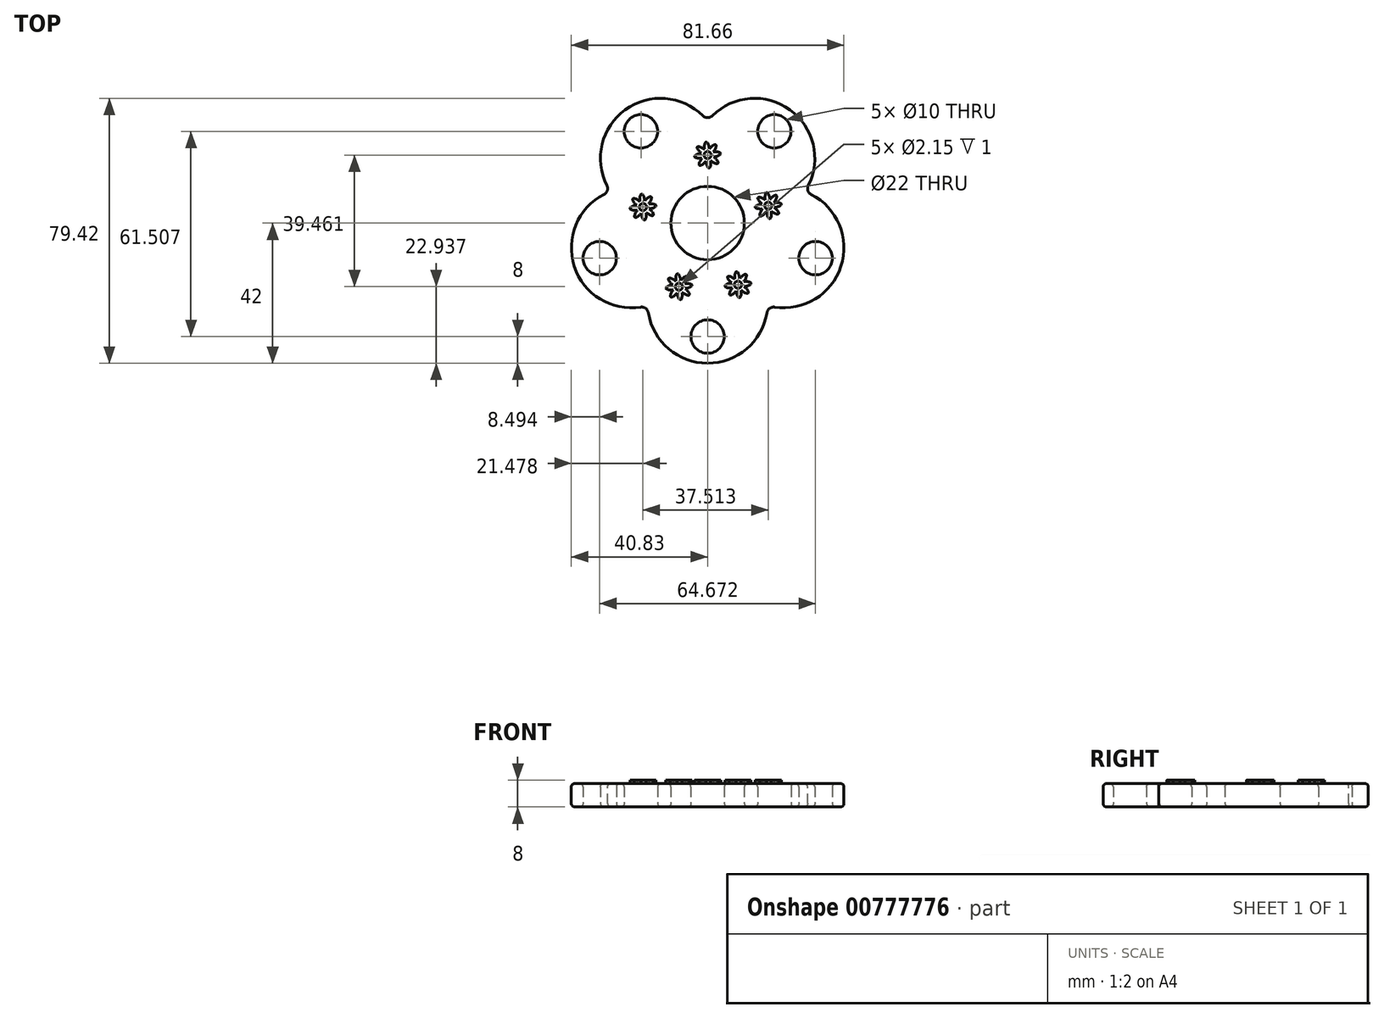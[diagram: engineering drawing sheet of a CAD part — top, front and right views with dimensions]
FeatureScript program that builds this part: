
annotation { "Feature Type Name" : "Feature", "Feature Type Description" : "" }
export const myFeature = defineFeature(function(context is Context, id is Id, definition is map)
    precondition{}
    {
        {
            var Q0;
            Q0=qCreatedBy(makeId("Top.planeOp"),FACE);
            var sketch = newSketch(context, id + "F0", { "sketchPlane" : qUnion([Q0])});
            skCircle(sketch, "E0.cCircle", {"center": v(0, 0) * mm, "radius": 24 * mm, "construction": true});
            skPoint(sketch, "E0.0.midPoint", {"position": v(14.1, 19.42) * mm});
            skArc(sketch, "E1", {"start": v(0, 30.6) * mm, "mid": v(-24.69, 33.98) * mm, "end": v(-29.1, 9.45) * mm});
            skArc(sketch, "E2", {"start": v(29.1, 9.45) * mm, "mid": v(24.69, 33.98) * mm, "end": v(0, 30.6) * mm});
            skArc(sketch, "E3", {"start": v(17.98, -24.75) * mm, "mid": v(39.94, -12.98) * mm, "end": v(29.1, 9.45) * mm});
            skArc(sketch, "E4", {"start": v(-17.98, -24.75) * mm, "mid": v(0, -42) * mm, "end": v(17.98, -24.75) * mm});
            skArc(sketch, "E5", {"start": v(-29.1, 9.45) * mm, "mid": v(-39.94, -12.98) * mm, "end": v(-17.98, -24.75) * mm});
            skCircle(sketch, "E6", {"center": v(0, 0) * mm, "radius": 30.6 * mm, "construction": true});
            skCircle(sketch, "E7", {"center": v(0, 0) * mm, "radius": 11 * mm});
            skCircle(sketch, "E8", {"center": v(-19.98, 27.5) * mm, "radius": 5 * mm});
            skCircle(sketch, "E9", {"center": v(19.98, 27.5) * mm, "radius": 5 * mm});
            skCircle(sketch, "E10", {"center": v(32.34, -10.5) * mm, "radius": 5 * mm});
            skCircle(sketch, "E11", {"center": v(0, -34) * mm, "radius": 5 * mm});
            skCircle(sketch, "E12", {"center": v(-32.34, -10.5) * mm, "radius": 5 * mm});
            skCircle(sketch, "E13", {"center": v(0, 0) * mm, "radius": 34 * mm, "construction": true});
            skLineSegment(sketch, "E14", {"start": v(0, 0) * mm, "end": v(0, 61.86) * mm, "construction": true});
            skLineSegment(sketch, "E15", {"start": v(0, 0) * mm, "end": v(37.88, 52.14) * mm, "construction": true});
            skLineSegment(sketch, "E16", {"start": v(0, 0) * mm, "end": v(75.05, -24.39) * mm, "construction": true});
            skLineSegment(sketch, "E17", {"start": v(0, 0) * mm, "end": v(0, -39) * mm, "construction": true});
            skLineSegment(sketch, "E18", {"start": v(0, 0) * mm, "end": v(-66.61, -21.64) * mm, "construction": true});
            skLineSegment(sketch, "E19", {"start": v(0, 0) * mm, "end": v(-34.54, 47.54) * mm, "construction": true});
            skSolve(sketch);
        }
        {
            var Q0;
            Q0=qSketchRegion(id+"F0",true);
            extrude(context, id + "F1", {"entities" : qUnion([Q0]), "depth" : 7 * mm, "offsetDistance" : 25.4 * mm});
        }
        {
            var Q0;
            Q0=makeQuery(id+"F1.opExtrude","SWEPT_EDGE",EDGE,{"disambiguationData":[OSD([sQuery(id+"F0.wireOp",EDGE,"E3"),sQuery(id+"F0.wireOp",EDGE,"E4")])]});
            var Q1;
            Q1=makeQuery(id+"F1.opExtrude","SWEPT_EDGE",EDGE,{"disambiguationData":[OSD([sQuery(id+"F0.wireOp",EDGE,"E2"),sQuery(id+"F0.wireOp",EDGE,"E3")])]});
            var Q2;
            Q2=makeQuery(id+"F1.opExtrude","SWEPT_EDGE",EDGE,{"disambiguationData":[OSD([sQuery(id+"F0.wireOp",EDGE,"E1"),sQuery(id+"F0.wireOp",EDGE,"E2")])]});
            var Q3;
            Q3=makeQuery(id+"F1.opExtrude","SWEPT_EDGE",EDGE,{"disambiguationData":[OSD([sQuery(id+"F0.wireOp",EDGE,"E1"),sQuery(id+"F0.wireOp",EDGE,"E5")])]});
            var Q4;
            Q4=makeQuery(id+"F1.opExtrude","SWEPT_EDGE",EDGE,{"disambiguationData":[OSD([sQuery(id+"F0.wireOp",EDGE,"E4"),sQuery(id+"F0.wireOp",EDGE,"E5")])]});
            fillet(context, id + "F2", {"entities" : qUnion([Q0, Q1, Q2, Q3, Q4]), "radius" : 2 * mm, "tangentPropagation" : true, "allowEdgeOverflow" : false});
        }
        {
            var Q0;
            Q0=makeQuery(id+"F1.opExtrude","CAP_FACE",FACE,{"disambiguationData":[OSD([sQuery(id+"F0.wireOp",EDGE,"E1"),sQuery(id+"F0.wireOp",EDGE,"E2"),sQuery(id+"F0.wireOp",EDGE,"E3"),sQuery(id+"F0.wireOp",EDGE,"E4"),sQuery(id+"F0.wireOp",EDGE,"E5"),sQuery(id+"F0.wireOp",EDGE,"E7"),sQuery(id+"F0.wireOp",EDGE,"E8"),sQuery(id+"F0.wireOp",EDGE,"E9"),sQuery(id+"F0.wireOp",EDGE,"E10"),sQuery(id+"F0.wireOp",EDGE,"E11"),sQuery(id+"F0.wireOp",EDGE,"E12")])],"isStart":false});
            var Q1;
            Q1=makeQuery(id+"F1.opExtrude","CAP_FACE",FACE,{"disambiguationData":[OSD([sQuery(id+"F0.wireOp",EDGE,"E1"),sQuery(id+"F0.wireOp",EDGE,"E2"),sQuery(id+"F0.wireOp",EDGE,"E3"),sQuery(id+"F0.wireOp",EDGE,"E4"),sQuery(id+"F0.wireOp",EDGE,"E5"),sQuery(id+"F0.wireOp",EDGE,"E7"),sQuery(id+"F0.wireOp",EDGE,"E8"),sQuery(id+"F0.wireOp",EDGE,"E9"),sQuery(id+"F0.wireOp",EDGE,"E10"),sQuery(id+"F0.wireOp",EDGE,"E11"),sQuery(id+"F0.wireOp",EDGE,"E12")])],"isStart":true});
            fillet(context, id + "F3", {"entities" : qUnion([Q0, Q1]), "radius" : 1 * mm, "tangentPropagation" : true, "allowEdgeOverflow" : false});
        }
        {
            var Q0;
            Q0=makeQuery(id+"F1.opExtrude","CAP_FACE",FACE,{"disambiguationData":[OSD([sQuery(id+"F0.wireOp",EDGE,"E1"),sQuery(id+"F0.wireOp",EDGE,"E2"),sQuery(id+"F0.wireOp",EDGE,"E3"),sQuery(id+"F0.wireOp",EDGE,"E4"),sQuery(id+"F0.wireOp",EDGE,"E5"),sQuery(id+"F0.wireOp",EDGE,"E7"),sQuery(id+"F0.wireOp",EDGE,"E8"),sQuery(id+"F0.wireOp",EDGE,"E9"),sQuery(id+"F0.wireOp",EDGE,"E10"),sQuery(id+"F0.wireOp",EDGE,"E11"),sQuery(id+"F0.wireOp",EDGE,"E12")])],"isStart":false});
            var sketch = newSketch(context, id + "F4", { "sketchPlane" : qUnion([Q0])});
            skEllipticalArc(sketch, "E20", {});
            skEllipticalArc(sketch, "E21.1.0", {});
            skEllipticalArc(sketch, "E21.2.0", {});
            skEllipticalArc(sketch, "E21.3.0", {});
            skEllipticalArc(sketch, "E21.4.0", {});
            skEllipticalArc(sketch, "E21.5.0", {});
            skEllipticalArc(sketch, "E21.6.0", {});
            skEllipticalArc(sketch, "E21.7.0", {});
            skPoint(sketch, "E21.center", {"position": v(0, 20.4) * mm});
            skPoint(sketch, "E22.orphan", {"position": v(-1.52, 20.99) * mm});
            skPoint(sketch, "E23.orphan", {"position": v(-0.88, 21.76) * mm});
            skPoint(sketch, "E24.orphan", {"position": v(-0.66, 21.89) * mm});
            skPoint(sketch, "E25.orphan", {"position": v(0.34, 21.99) * mm});
            skPoint(sketch, "E26.orphan", {"position": v(-1.6, 20.74) * mm});
            skPoint(sketch, "E27.orphan", {"position": v(-1.37, 19.51) * mm});
            skPoint(sketch, "E28.orphan", {"position": v(-1.49, 19.74) * mm});
            skPoint(sketch, "E29.orphan", {"position": v(-0.59, 18.88) * mm});
            skPoint(sketch, "E30.orphan", {"position": v(0.66, 18.9) * mm});
            skPoint(sketch, "E31.orphan", {"position": v(0.88, 19.03) * mm});
            skPoint(sketch, "E32.orphan", {"position": v(1.6, 20.06) * mm});
            skPoint(sketch, "E33.orphan", {"position": v(1.37, 21.28) * mm});
            skPoint(sketch, "E34.orphan", {"position": v(0.59, 21.92) * mm});
            skCircle(sketch, "E35", {"center": v(0, 20.4) * mm, "radius": 1.07 * mm});
            skEllipticalArc(sketch, "E36", {});
            skEllipticalArc(sketch, "E37.1.0", {});
            skEllipticalArc(sketch, "E37.2.0", {});
            skEllipticalArc(sketch, "E37.3.0", {});
            skEllipticalArc(sketch, "E37.4.0", {});
            skEllipticalArc(sketch, "E37.5.0", {});
            skEllipticalArc(sketch, "E37.6.0", {});
            skEllipticalArc(sketch, "E37.7.0", {});
            skPoint(sketch, "E37.center", {"position": v(-19.35, 4.81) * mm});
            skPoint(sketch, "E38.orphan", {"position": v(-20.87, 5.4) * mm});
            skPoint(sketch, "E39.orphan", {"position": v(-20.24, 6.18) * mm});
            skPoint(sketch, "E40.orphan", {"position": v(-20, 6.3) * mm});
            skPoint(sketch, "E41.orphan", {"position": v(-19.01, 6.4) * mm});
            skPoint(sketch, "E42.orphan", {"position": v(-20.94, 5.15) * mm});
            skPoint(sketch, "E43.orphan", {"position": v(-20.72, 3.93) * mm});
            skPoint(sketch, "E44.orphan", {"position": v(-20.84, 4.15) * mm});
            skPoint(sketch, "E45.orphan", {"position": v(-19.94, 3.3) * mm});
            skPoint(sketch, "E46.orphan", {"position": v(-18.7, 3.32) * mm});
            skPoint(sketch, "E47.orphan", {"position": v(-18.47, 3.45) * mm});
            skPoint(sketch, "E48.orphan", {"position": v(-17.76, 4.47) * mm});
            skPoint(sketch, "E49.orphan", {"position": v(-17.99, 5.7) * mm});
            skPoint(sketch, "E50.orphan", {"position": v(-18.76, 6.33) * mm});
            skCircle(sketch, "E51", {"center": v(-19.35, 4.81) * mm, "radius": 1.07 * mm});
            skEllipticalArc(sketch, "E52", {});
            skEllipticalArc(sketch, "E53.1.0", {});
            skEllipticalArc(sketch, "E53.2.0", {});
            skEllipticalArc(sketch, "E53.3.0", {});
            skEllipticalArc(sketch, "E53.4.0", {});
            skEllipticalArc(sketch, "E53.5.0", {});
            skEllipticalArc(sketch, "E53.6.0", {});
            skEllipticalArc(sketch, "E53.7.0", {});
            skPoint(sketch, "E53.center", {"position": v(18.16, 5.23) * mm});
            skPoint(sketch, "E54.orphan", {"position": v(16.64, 5.82) * mm});
            skPoint(sketch, "E55.orphan", {"position": v(17.28, 6.6) * mm});
            skPoint(sketch, "E56.orphan", {"position": v(17.5, 6.72) * mm});
            skPoint(sketch, "E57.orphan", {"position": v(18.5, 6.82) * mm});
            skPoint(sketch, "E58.orphan", {"position": v(16.57, 5.57) * mm});
            skPoint(sketch, "E59.orphan", {"position": v(16.8, 4.34) * mm});
            skPoint(sketch, "E60.orphan", {"position": v(16.67, 4.57) * mm});
            skPoint(sketch, "E61.orphan", {"position": v(17.57, 3.7) * mm});
            skPoint(sketch, "E62.orphan", {"position": v(18.82, 3.74) * mm});
            skPoint(sketch, "E63.orphan", {"position": v(19.04, 3.86) * mm});
            skPoint(sketch, "E64.orphan", {"position": v(19.75, 4.89) * mm});
            skPoint(sketch, "E65.orphan", {"position": v(19.53, 6.11) * mm});
            skPoint(sketch, "E66.orphan", {"position": v(18.75, 6.74) * mm});
            skCircle(sketch, "E67", {"center": v(18.16, 5.23) * mm, "radius": 1.07 * mm});
            skEllipticalArc(sketch, "E68", {});
            skEllipticalArc(sketch, "E69.1.0", {});
            skEllipticalArc(sketch, "E69.2.0", {});
            skEllipticalArc(sketch, "E69.3.0", {});
            skEllipticalArc(sketch, "E69.4.0", {});
            skEllipticalArc(sketch, "E69.5.0", {});
            skEllipticalArc(sketch, "E69.6.0", {});
            skEllipticalArc(sketch, "E69.7.0", {});
            skPoint(sketch, "E69.center", {"position": v(9.1, -18.47) * mm});
            skPoint(sketch, "E70.orphan", {"position": v(7.58, -17.88) * mm});
            skPoint(sketch, "E71.orphan", {"position": v(8.21, -17.1) * mm});
            skPoint(sketch, "E72.orphan", {"position": v(8.44, -16.98) * mm});
            skPoint(sketch, "E73.orphan", {"position": v(9.44, -16.88) * mm});
            skPoint(sketch, "E74.orphan", {"position": v(7.5, -18.13) * mm});
            skPoint(sketch, "E75.orphan", {"position": v(7.73, -19.35) * mm});
            skPoint(sketch, "E76.orphan", {"position": v(7.6, -19.13) * mm});
            skPoint(sketch, "E77.orphan", {"position": v(8.51, -19.99) * mm});
            skPoint(sketch, "E78.orphan", {"position": v(9.76, -19.96) * mm});
            skPoint(sketch, "E79.orphan", {"position": v(9.98, -19.84) * mm});
            skPoint(sketch, "E80.orphan", {"position": v(10.69, -18.81) * mm});
            skPoint(sketch, "E81.orphan", {"position": v(10.46, -17.59) * mm});
            skPoint(sketch, "E82.orphan", {"position": v(9.69, -16.95) * mm});
            skCircle(sketch, "E83", {"center": v(9.1, -18.47) * mm, "radius": 1.07 * mm});
            skEllipticalArc(sketch, "E84", {});
            skEllipticalArc(sketch, "E85.1.0", {});
            skEllipticalArc(sketch, "E85.2.0", {});
            skEllipticalArc(sketch, "E85.3.0", {});
            skEllipticalArc(sketch, "E85.4.0", {});
            skEllipticalArc(sketch, "E85.5.0", {});
            skEllipticalArc(sketch, "E85.6.0", {});
            skEllipticalArc(sketch, "E85.7.0", {});
            skPoint(sketch, "E85.center", {"position": v(-8.6, -19.06) * mm});
            skPoint(sketch, "E86.orphan", {"position": v(-10.1, -18.48) * mm});
            skPoint(sketch, "E87.orphan", {"position": v(-9.48, -17.7) * mm});
            skPoint(sketch, "E88.orphan", {"position": v(-9.25, -17.57) * mm});
            skPoint(sketch, "E89.orphan", {"position": v(-8.25, -17.47) * mm});
            skPoint(sketch, "E90.orphan", {"position": v(-10.18, -18.72) * mm});
            skPoint(sketch, "E91.orphan", {"position": v(-9.96, -19.95) * mm});
            skPoint(sketch, "E92.orphan", {"position": v(-10.08, -19.72) * mm});
            skPoint(sketch, "E93.orphan", {"position": v(-9.18, -20.58) * mm});
            skPoint(sketch, "E94.orphan", {"position": v(-7.93, -20.55) * mm});
            skPoint(sketch, "E95.orphan", {"position": v(-7.7, -20.43) * mm});
            skPoint(sketch, "E96.orphan", {"position": v(-7, -19.4) * mm});
            skPoint(sketch, "E97.orphan", {"position": v(-7.23, -18.18) * mm});
            skPoint(sketch, "E98.orphan", {"position": v(-8, -17.55) * mm});
            skCircle(sketch, "E99", {"center": v(-8.6, -19.06) * mm, "radius": 1.07 * mm});
            const initialGuessF4  = {"E20": [0.0010247566278231382, 0.02166222113838485, 0.6140089271210712, 0.7892990798269254, 0.0023157442023888897, 0.0007414824988597866, 4.775112420753962, 1.4962821796103536], "E21.1.0": [-0.00016934392095610713, 0.022016544682995458, -0.1239488556535351, 0.9922886078063071, 0.0023157442023888897, 0.0007414824988597866, 4.7751124207539615, 1.4962821796103567], "E21.2.0": [-0.0012642450975447021, 0.021422732668663284, -0.7892990798269255, 0.614008927121071, 0.0023157442023888897, 0.0007414824988597866, 4.775112420753961, 1.4962821796103531], "E21.3.0": [-0.0016185686421553084, 0.02022863211988404, -0.9922886078063071, -0.12394885565353492, 0.0023157442023888897, 0.0007414824988597866, 4.775112420753962, 1.496282179610354], "E21.4.0": [-0.0010247566278231385, 0.019133730943295447, -0.614008927121071, -0.7892990798269255, 0.0023157442023888897, 0.0007414824988597866, 4.7751124207539615, 1.4962821796103547], "E21.5.0": [0.00016934392095610713, 0.01877940739868484, 0.12394885565353497, -0.9922886078063071, 0.0023157442023888897, 0.0007414824988597866, 4.77511242075396, 1.4962821796103551], "E21.6.0": [0.0012642450975447021, 0.01937321941301701, 0.7892990798269254, -0.6140089271210711, 0.0023157442023888897, 0.0007414824988597866, 4.775112420753961, 1.4962821796103563], "E21.7.0": [0.0016185686421553084, 0.020567319961796258, 0.9922886078063071, 0.12394885565353492, 0.0023157442023888897, 0.0007414824988597866, 4.77511242075396, 1.4962821796103547], "E36": [-0.01832736750656251, 0.006076403150645358, 0.6140089271210712, 0.7892990798269254, 0.0023157442023888897, 0.0007414824988597866, 4.7751124207539615, 1.4962821796103527], "E37.1.0": [-0.019521468055341756, 0.006430726695255965, -0.1239488556535351, 0.9922886078063071, 0.0023157442023888897, 0.0007414824988597866, 4.7751124207539615, 1.4962821796103567], "E37.2.0": [-0.020616369231930352, 0.005836914680923792, -0.7892990798269255, 0.614008927121071, 0.0023157442023888897, 0.0007414824988597866, 4.775112420753961, 1.4962821796103531], "E37.3.0": [-0.02097069277654096, 0.004642814132144547, -0.9922886078063071, -0.12394885565353492, 0.0023157442023888897, 0.0007414824988597866, 4.775112420753963, 1.4962821796103538], "E37.4.0": [-0.02037688076220879, 0.0035479129555559545, -0.614008927121071, -0.7892990798269255, 0.0023157442023888897, 0.0007414824988597866, 4.775112420753961, 1.496282179610355], "E37.5.0": [-0.019182780213429545, 0.0031935894109453478, 0.12394885565353497, -0.9922886078063071, 0.0023157442023888897, 0.0007414824988597866, 4.77511242075396, 1.4962821796103551], "E37.6.0": [-0.018087879036840948, 0.0037874014252775178, 0.7892990798269254, -0.6140089271210711, 0.0023157442023888897, 0.0007414824988597866, 4.775112420753961, 1.4962821796103551], "E37.7.0": [-0.01773355549223034, 0.004981501974056765, 0.9922886078063071, 0.12394885565353492, 0.0023157442023888897, 0.0007414824988597866, 4.775112420753958, 1.4962821796103551], "E52": [0.019185944400784024, 0.00649146601261529, 0.6140089271210712, 0.7892990798269254, 0.0023157442023888897, 0.0007414824988597866, 4.775112420753962, 1.4962821796103538], "E53.1.0": [0.01799184385200478, 0.006845789557225897, -0.1239488556535351, 0.9922886078063071, 0.0023157442023888897, 0.0007414824988597866, 4.7751124207539615, 1.4962821796103567], "E53.2.0": [0.016896942675416183, 0.006251977542893724, -0.7892990798269255, 0.614008927121071, 0.0023157442023888897, 0.0007414824988597866, 4.775112420753961, 1.4962821796103531], "E53.3.0": [0.016542619130805576, 0.005057876994114479, -0.9922886078063071, -0.12394885565353492, 0.0023157442023888897, 0.0007414824988597866, 4.775112420753962, 1.4962821796103538], "E53.4.0": [0.017136431145137746, 0.003962975817525886, -0.614008927121071, -0.7892990798269255, 0.0023157442023888897, 0.0007414824988597866, 4.7751124207539615, 1.496282179610355], "E53.5.0": [0.01833053169391699, 0.0036086522729152793, 0.12394885565353497, -0.9922886078063071, 0.0023157442023888897, 0.0007414824988597866, 4.77511242075396, 1.4962821796103551], "E53.6.0": [0.019425432870505587, 0.004202464287247449, 0.7892990798269254, -0.6140089271210711, 0.0023157442023888897, 0.0007414824988597866, 4.775112420753961, 1.4962821796103565], "E53.7.0": [0.019779756415116194, 0.005396564836026697, 0.9922886078063071, 0.12394885565353492, 0.0023157442023888897, 0.0007414824988597866, 4.77511242075396, 1.4962821796103551], "E68": [0.010122740116026648, -0.017205620597284706, 0.6140089271210712, 0.7892990798269254, 0.0023157442023888897, 0.0007414824988597866, 4.7751124207539615, 1.4962821796103536], "E69.1.0": [0.008928639567247402, -0.0168512970526741, -0.1239488556535351, 0.9922886078063071, 0.0023157442023888897, 0.0007414824988597866, 4.7751124207539615, 1.4962821796103567], "E69.2.0": [0.007833738390658807, -0.017445109067006272, -0.7892990798269255, 0.614008927121071, 0.0023157442023888897, 0.0007414824988597866, 4.775112420753961, 1.496282179610353], "E69.3.0": [0.0074794148460482004, -0.018639209615785517, -0.9922886078063071, -0.12394885565353492, 0.0023157442023888897, 0.0007414824988597866, 4.775112420753962, 1.4962821796103538], "E69.4.0": [0.00807322686038037, -0.01973411079237411, -0.614008927121071, -0.7892990798269255, 0.0023157442023888897, 0.0007414824988597866, 4.7751124207539615, 1.4962821796103547], "E69.5.0": [0.009267327409159616, -0.020088434336984717, 0.12394885565353497, -0.9922886078063071, 0.0023157442023888897, 0.0007414824988597866, 4.77511242075396, 1.4962821796103551], "E69.6.0": [0.010362228585748211, -0.019494622322652547, 0.7892990798269254, -0.6140089271210711, 0.0023157442023888897, 0.0007414824988597866, 4.77511242075396, 1.4962821796103558], "E69.7.0": [0.010716552130358818, -0.0183005217738733, 0.9922886078063071, 0.12394885565353492, 0.0023157442023888897, 0.0007414824988597866, 4.775112420753959, 1.4962821796103545], "E84": [-0.00756716827297544, -0.017798690642450207, 0.6140089271210712, 0.7892990798269254, 0.0023157442023888897, 0.0007414824988597866, 4.7751124207539615, 1.4962821796103527], "E85.1.0": [-0.00876126882175468, -0.0174443670978396, -0.1239488556535351, 0.9922886078063071, 0.0023157442023888897, 0.0007414824988597866, 4.7751124207539615, 1.4962821796103567], "E85.2.0": [-0.009856169998343274, -0.018038179112171773, -0.7892990798269255, 0.614008927121071, 0.0023157442023888897, 0.0007414824988597866, 4.77511242075396, 1.4962821796103527], "E85.3.0": [-0.010210493542953884, -0.019232279660951018, -0.9922886078063071, -0.12394885565353492, 0.0023157442023888897, 0.0007414824988597866, 4.775112420753963, 1.4962821796103536], "E85.4.0": [-0.00961668152862171, -0.02032718083753961, -0.614008927121071, -0.7892990798269255, 0.0023157442023888897, 0.0007414824988597866, 4.775112420753961, 1.4962821796103538], "E85.5.0": [-0.00842258097984247, -0.020681504382150218, 0.12394885565353497, -0.9922886078063071, 0.0023157442023888897, 0.0007414824988597866, 4.77511242075396, 1.4962821796103551], "E85.6.0": [-0.007327679803253877, -0.020087692367818048, 0.7892990798269254, -0.6140089271210711, 0.0023157442023888897, 0.0007414824988597866, 4.77511242075396, 1.496282179610357], "E85.7.0": [-0.0069733562586432665, -0.0188935918190388, 0.9922886078063071, 0.12394885565353492, 0.0023157442023888897, 0.0007414824988597866, 4.77511242075396, 1.4962821796103536]};
            skSetInitialGuess(sketch, initialGuessF4);
            skSolve(sketch);
        }
        {
            var Q0;
            Q0=qSketchRegion(id+"F4",true);
            extrude(context, id + "F5", {"entities" : qUnion([Q0]), "operationType" : NewBodyOperationType.ADD, "depth" : 1 * mm, "offsetDistance" : 25 * mm});
        }
    });
